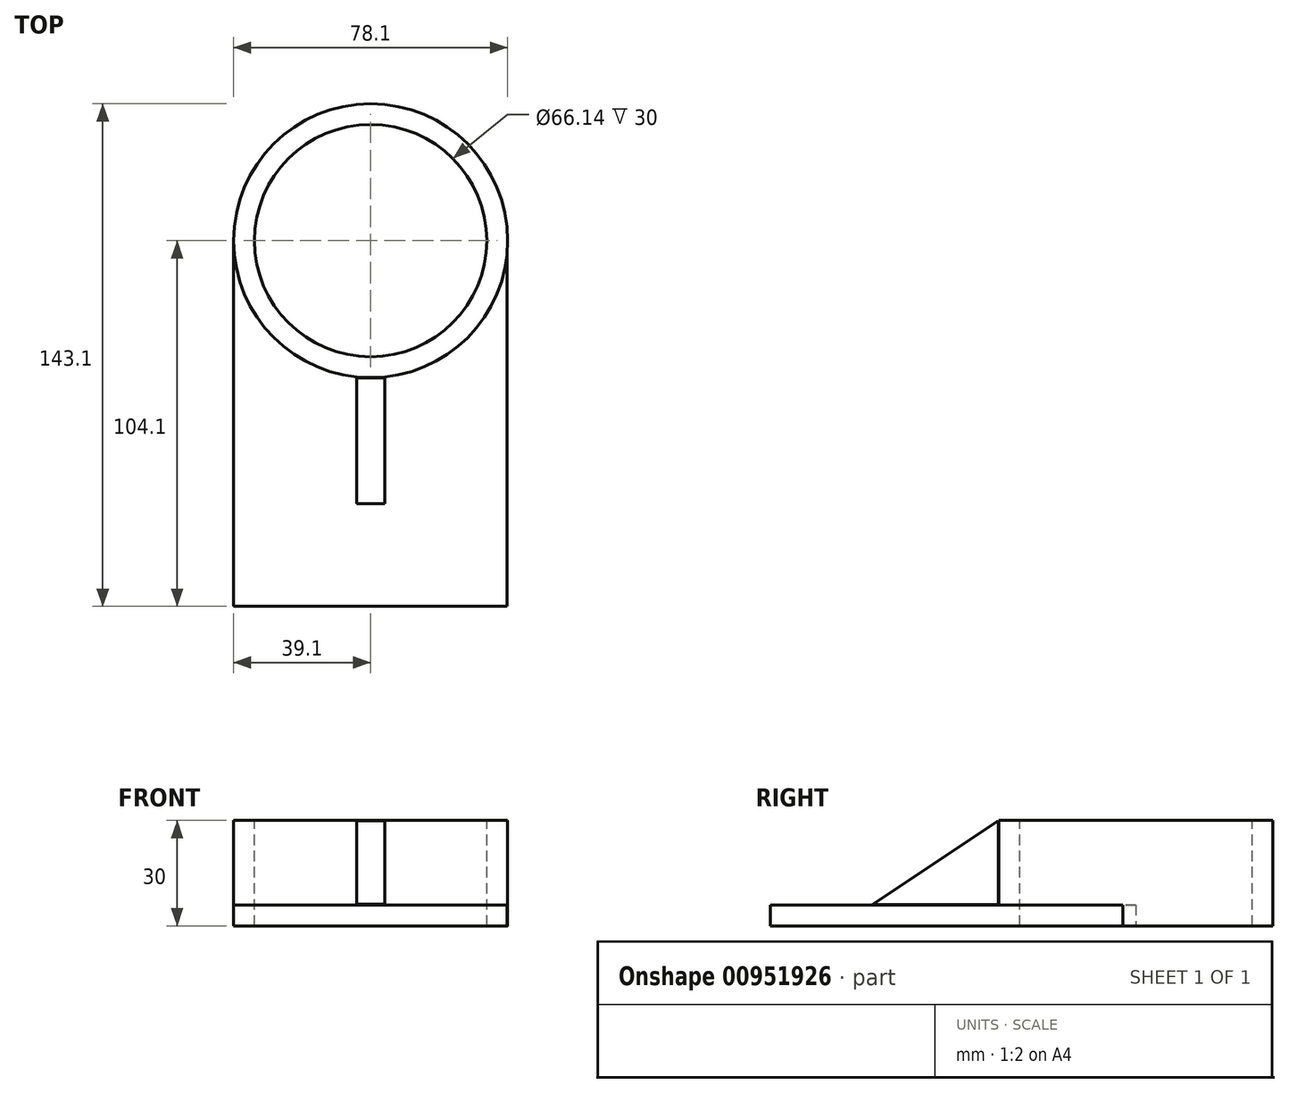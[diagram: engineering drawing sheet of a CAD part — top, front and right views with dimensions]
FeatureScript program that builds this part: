
annotation { "Feature Type Name" : "Feature", "Feature Type Description" : "" }
export const myFeature = defineFeature(function(context is Context, id is Id, definition is map)
    precondition{}
    {
        {
            var Q0;
            Q0=qCreatedBy(makeId("Top.planeOp"),FACE);
            var sketch = newSketch(context, id + "F0", { "sketchPlane" : qUnion([Q0])});
            skCircle(sketch, "E0", {"center": v(0, 0) * mm, "radius": 39 * mm});
            skSolve(sketch);
        }
        {
            var Q0;
            Q0 = qSketchRegion(id + "F0", true);
            var Q1;
            Q1=makeQuery(id+"F0.imprint","IMPRINT",FACE,{"disambiguationData":[TD([[makeQuery(id+"F0.imprint","IMPRINT",EDGE,{"derivedFrom":sQuery(id+"F0.wireOp",EDGE,"E0")}),1.0]])]});
            extrude(context, id + "F1", {"entities" : qUnion([Q0, Q1]), "depth" : 30 * mm, "offsetDistance" : 25 * mm});
        }
        {
            var Q0;
            Q0=qCreatedBy(makeId("Front.planeOp"),FACE);
            var sketch = newSketch(context, id + "F2", { "sketchPlane" : qUnion([Q0])});
            skLineSegment(sketch, "E1.bottom", {"start": v(-39.1, 0) * mm, "end": v(38.82, 0) * mm});
            skLineSegment(sketch, "E1.top", {"start": v(-39.1, 5.94) * mm, "end": v(38.82, 5.94) * mm});
            skLineSegment(sketch, "E1.left", {"start": v(-39.1, 0) * mm, "end": v(-39.1, 5.94) * mm});
            skLineSegment(sketch, "E1.right", {"start": v(38.82, 0) * mm, "end": v(38.82, 5.94) * mm});
            skSolve(sketch);
        }
        {
            var Q0;
            Q0 = qSketchRegion(id + "F2", true);
            extrude(context, id + "F3", {"entities" : qUnion([Q0]), "operationType" : NewBodyOperationType.ADD, "depth" : 74.5 * mm, "offsetDistance" : 25 * mm});
        }
        {
            var Q0;
            Q0=makeQuery(id+"F1.opExtrude","CAP_FACE",FACE,{"disambiguationData":[OSD([sQuery(id+"F0.wireOp",EDGE,"E0")])],"isStart":false});
            var sketch = newSketch(context, id + "F4", { "sketchPlane" : qUnion([Q0])});
            skCircle(sketch, "E2", {"center": v(0, 0) * mm, "radius": 33.07 * mm});
            skSolve(sketch);
        }
        {
            var Q0;
            Q0=makeQuery(id+"F4.imprint","IMPRINT",FACE,{"disambiguationData":[TD([[makeQuery(id+"F4.imprint","IMPRINT",EDGE,{"derivedFrom":sQuery(id+"F4.wireOp",EDGE,"E2")}),1.0]])]});
            extrude(context, id + "F5", {"entities" : qUnion([Q0]), "operationType" : NewBodyOperationType.REMOVE, "oppositeDirection" : true, "depth" : 30 * mm, "offsetDistance" : 25 * mm});
        }
        {
            var Q0;
            Q0=qCreatedBy(makeId("Right.planeOp"),FACE);
            var sketch = newSketch(context, id + "F6", { "sketchPlane" : qUnion([Q0])});
            skLineSegment(sketch, "E3", {"start": v(0, -74.77) * mm, "end": v(0, -39.02) * mm});
            skPoint(sketch, "E4.endSnap0", {"position": v(20.14, -31.65) * mm});
            skLineSegment(sketch, "E5", {"start": v(-74.88, 6.16) * mm, "end": v(-39.09, 29.92) * mm});
            skLineSegment(sketch, "E6", {"start": v(-39.09, 29.92) * mm, "end": v(-39.09, 6) * mm});
            skLineSegment(sketch, "E7", {"start": v(-39.09, 6) * mm, "end": v(-74.88, 6.16) * mm});
            skSolve(sketch);
        }
        {
            var Q0;
            Q0 = qSketchRegion(id + "F6", true);
            extrude(context, id + "F7", {"entities" : qUnion([Q0]), "oppositeDirection" : true, "depth" : 8 * mm, "offsetDistance" : 25 * mm, "symmetric" : true});
        }
        {
            var Q0;
            Q0=makeQuery(id+"F3.opExtrude","CAP_FACE",FACE,{"disambiguationData":[OSD([sQuery(id+"F2.wireOp",EDGE,"E1.bottom"),sQuery(id+"F2.wireOp",EDGE,"E1.top"),sQuery(id+"F2.wireOp",EDGE,"E1.left"),sQuery(id+"F2.wireOp",EDGE,"E1.right")])],"isStart":false});
            var sketch = newSketch(context, id + "F8", { "sketchPlane" : qUnion([Q0])});
            skSolve(sketch);
        }
        {
            var Q0;
            Q0 = qSketchRegion(id + "F8", true);
            var Q1;
            Q1=makeQuery(id+"F8.imprint","IMPRINT",FACE,{"disambiguationData":[TD([[makeQuery(id+"F8.imprint","IMPRINT",EDGE,{"derivedFrom":makeQuery(id+"F3.opExtrude","CAP_EDGE",EDGE,{"disambiguationData":[OSD([sQuery(id+"F2.wireOp",EDGE,"E1.bottom")])],"isStart":false})}),1.0]])]});
            extrude(context, id + "F9", {"entities" : qUnion([Q0, Q1]), "operationType" : NewBodyOperationType.ADD, "depth" : 29.6 * mm, "offsetDistance" : 25 * mm});
        }
    });
